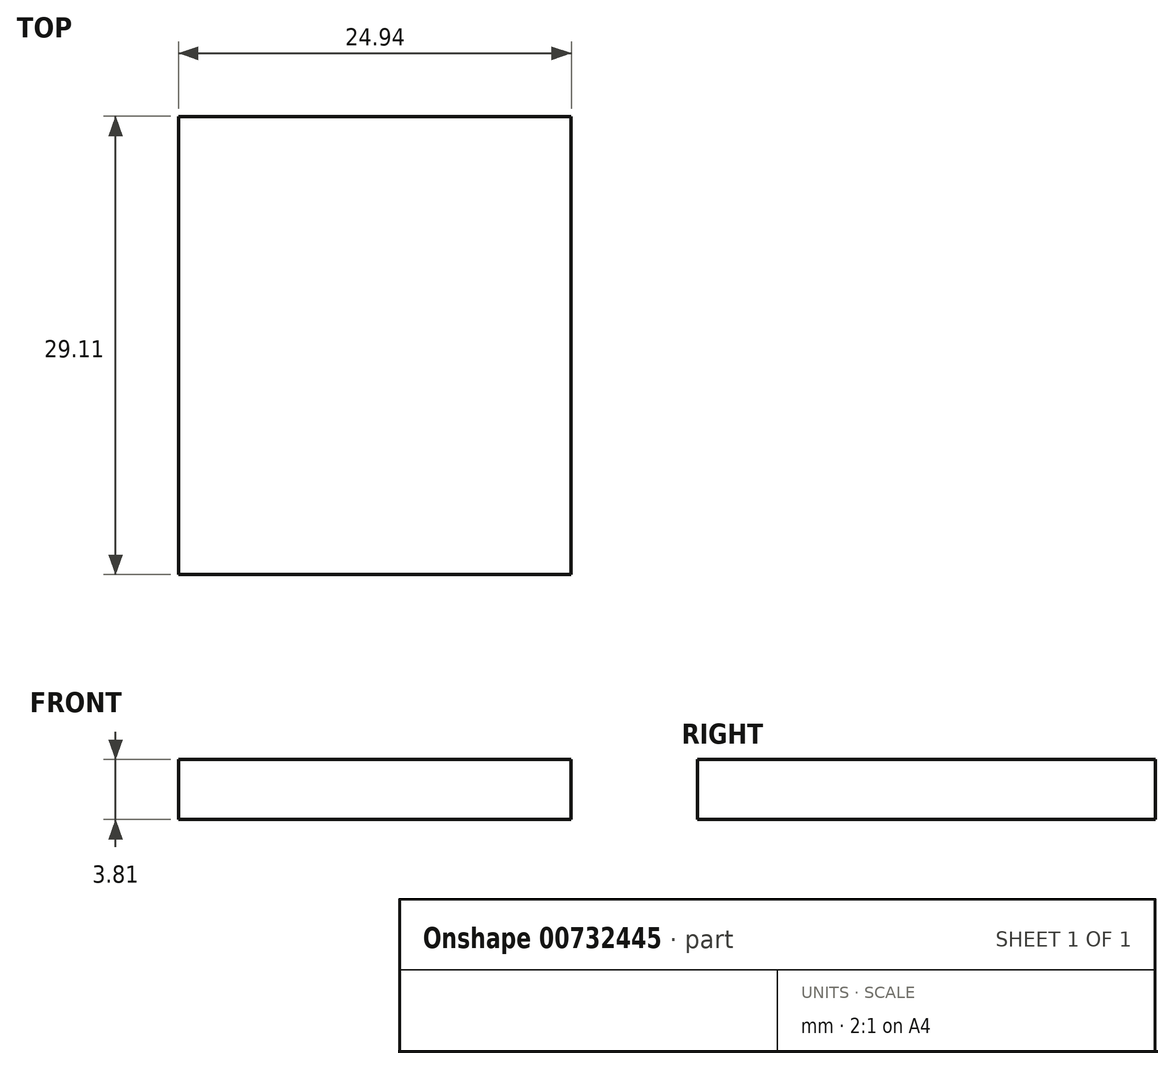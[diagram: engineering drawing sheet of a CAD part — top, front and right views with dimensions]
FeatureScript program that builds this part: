
annotation { "Feature Type Name" : "Feature", "Feature Type Description" : "" }
export const myFeature = defineFeature(function(context is Context, id is Id, definition is map)
    precondition{}
    {
        {
            var Q0;
            Q0=qCreatedBy(makeId("Top.planeOp"),FACE);
            var sketch = newSketch(context, id + "F0", { "sketchPlane" : qUnion([Q0])});
            skLineSegment(sketch, "E0.bottom", {"start": v(0, 0) * mm, "end": v(24.94, 0) * mm});
            skLineSegment(sketch, "E0.top", {"start": v(0, 29.1) * mm, "end": v(24.94, 29.1) * mm});
            skLineSegment(sketch, "E0.left", {"start": v(0, 0) * mm, "end": v(0, 29.1) * mm});
            skLineSegment(sketch, "E0.right", {"start": v(24.94, 0) * mm, "end": v(24.94, 29.1) * mm});
            skSolve(sketch);
        }
        {
            var Q0;
            Q0=makeQuery(id+"F0.imprint","IMPRINT",FACE,{"disambiguationData":[TD([[makeQuery(id+"F0.imprint","IMPRINT",EDGE,{"derivedFrom":sQuery(id+"F0.wireOp",EDGE,"E0.bottom")}),1.0]])]});
            extrude(context, id + "F1", {"entities" : qUnion([Q0]), "depth" : 3.8 * mm, "offsetDistance" : 25.4 * mm});
        }
    });
